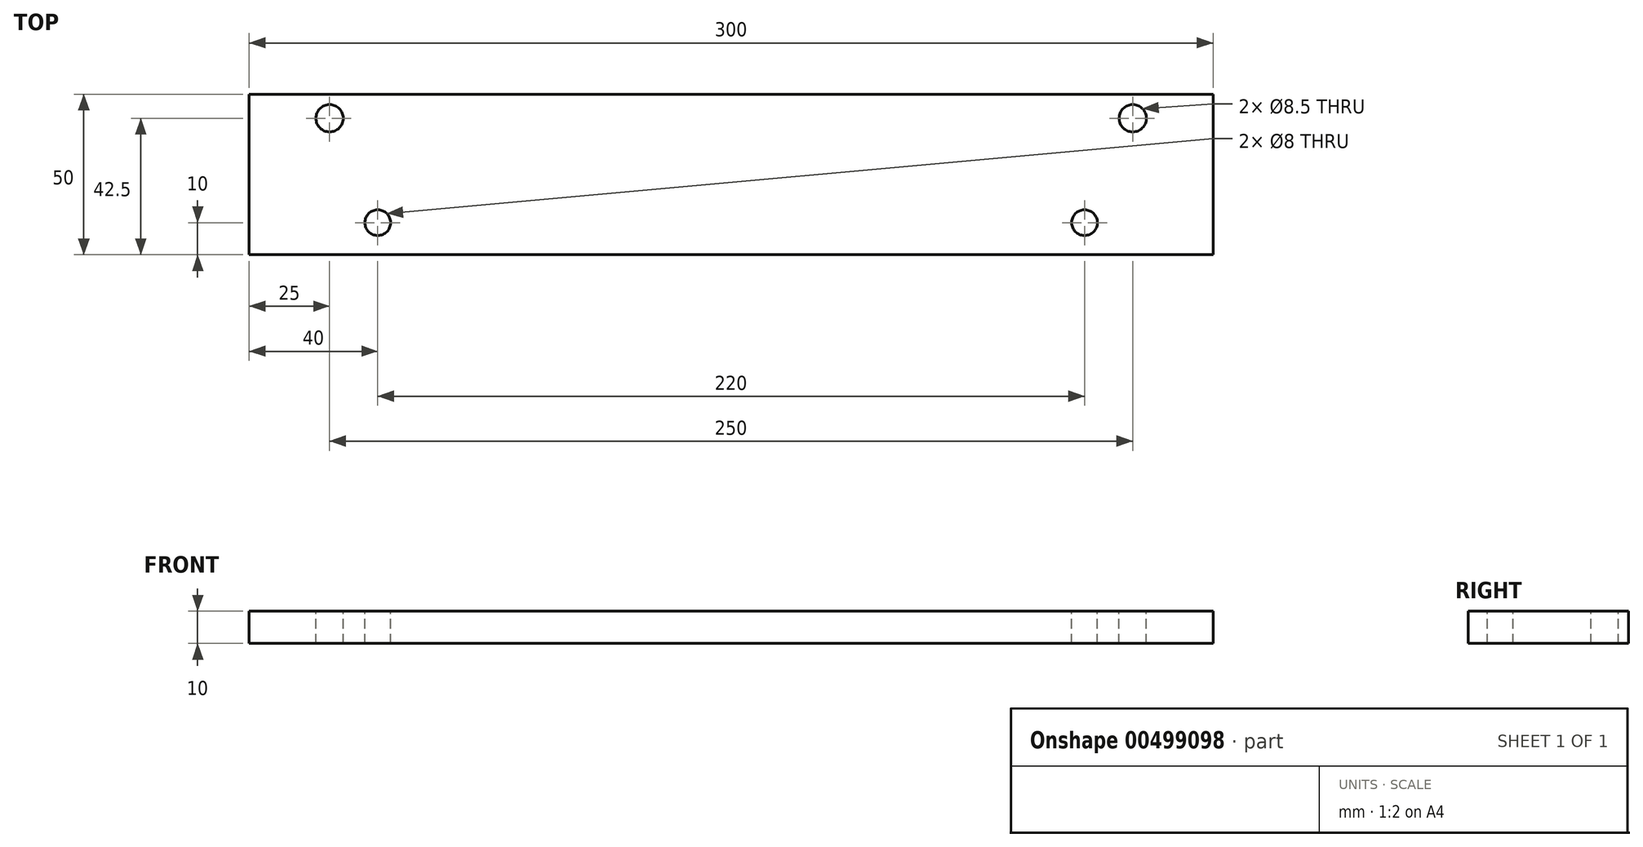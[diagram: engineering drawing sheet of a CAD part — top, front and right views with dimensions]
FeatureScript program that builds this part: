
annotation { "Feature Type Name" : "Feature", "Feature Type Description" : "" }
export const myFeature = defineFeature(function(context is Context, id is Id, definition is map)
    precondition{}
    {
        {
            var Q0;
            Q0=qCreatedBy(makeId("Right.planeOp"),FACE);
            var sketch = newSketch(context, id + "F0", { "sketchPlane" : qUnion([Q0])});
            skLineSegment(sketch, "E0.bottom", {"start": v(25, -5) * mm, "end": v(-25, -5) * mm});
            skLineSegment(sketch, "E0.top", {"start": v(25, 5) * mm, "end": v(-25, 5) * mm});
            skLineSegment(sketch, "E0.left", {"start": v(25, -5) * mm, "end": v(25, 5) * mm});
            skLineSegment(sketch, "E0.right", {"start": v(-25, -5) * mm, "end": v(-25, 5) * mm});
            skPoint(sketch, "E0.middle", {"position": v(0, 0) * mm});
            skSolve(sketch);
        }
        {
            var Q0;
            Q0=makeQuery(id+"F0.imprint","IMPRINT",FACE,{"disambiguationData":[TD([[makeQuery(id+"F0.imprint","IMPRINT",EDGE,{"derivedFrom":sQuery(id+"F0.wireOp",EDGE,"E0.bottom")}),-1.0]])]});
            extrude(context, id + "F1", {"entities" : qUnion([Q0]), "depth" : 300 * mm});
        }
        {
            var Q0;
            Q0=makeQuery(id+"F1.opExtrude","SWEPT_FACE",FACE,{"disambiguationData":[OSD([sQuery(id+"F0.wireOp",EDGE,"E0.top")])]});
            var sketch = newSketch(context, id + "F2", { "sketchPlane" : qUnion([Q0])});
            skCircle(sketch, "E1", {"center": v(25, 17.5) * mm, "radius": 4.25 * mm});
            skCircle(sketch, "E2", {"center": v(275, 17.5) * mm, "radius": 4.25 * mm});
            skSolve(sketch);
        }
        {
            var Q0;
            Q0 = qSketchRegion(id + "F2", true);
            extrude(context, id + "F3", {"entities" : qUnion([Q0]), "operationType" : NewBodyOperationType.REMOVE, "oppositeDirection" : true, "depth" : 25 * mm});
        }
        {
            var Q0;
            Q0=makeQuery(id+"F1.opExtrude","SWEPT_FACE",FACE,{"disambiguationData":[OSD([sQuery(id+"F0.wireOp",EDGE,"E0.top")])]});
            var sketch = newSketch(context, id + "F4", { "sketchPlane" : qUnion([Q0])});
            skCircle(sketch, "E3", {"center": v(40, -15) * mm, "radius": 4 * mm});
            skCircle(sketch, "E4", {"center": v(260, -15) * mm, "radius": 4 * mm});
            skSolve(sketch);
        }
        {
            var Q0;
            Q0 = qSketchRegion(id + "F4", true);
            extrude(context, id + "F5", {"entities" : qUnion([Q0]), "operationType" : NewBodyOperationType.REMOVE, "oppositeDirection" : true, "depth" : 329 * mm});
        }
    });
